# Revit family: PS0810
name_source: partatom
category: Luminarias
units: mm (PartAtom-declared; Revit-internal decimal feet)

## family parameters
Compartido = Sí
Corte con vacíos al cargar = No
Cota de conector redondo = Diámetro de uso
Origen de luz = No
Punto de cálculo de habitación = No
Se basa en plano de trabajo = Sí
Siempre vertical = No
Tipo de pieza = Normal

## types (1)
- PERFIL_PS0810
    Clips de Sujecion 0810.2 = 4
    Descripción = PERFIL DE ALUMINIO CON DIFUSOR LECHOSO, PARA ALOJAR TIRA LUMINOSA DE HASTA 6.2MM DE ANCHO. INSTALACION SOBRE SUPERFICIES PLANAS, PERFIL DE CLIP MONTADO. IDEAL PARA ATENUAR EL BRILLO E INCORPORAR LA LUZ AL AMBIENTE.PRESENTACION DESDE 0.5 - 3 METROS, REQUEIRE ACCESORIOS COMO TAPA FINAL (CONSIDERAR 1 POR SEGMENTO DE PERFIL), CLIPS DE SUJECION LINEAL (CONSIDERAR 4 PZAS POR 1M DE PERFIL)
    Elevación por defecto = 1219 mm
    Fabricante = BRILLANT
    Longitud = 1000 mm  [stored 3.28084 ft]
    Modelo = PS0810
    Tapa Final 0810.1 = 1

note: [stored X ft] marks values corroborated as IEEE doubles in the binary element streams (Revit-internal decimal feet)

## geometry (parser evidence)
native form markers: Blend x2
no freeform markers — native parametric forms only
